# Revit family: Hushwall_2_EN
name_source: partatom
category: Casework
units: mm (PartAtom-declared; Revit-internal decimal feet)

## family parameters
Always vertical = Yes
Cut with Voids When Loaded = No
OmniClass Number = 23.40.35.00
OmniClass Title = Casework
Room Calculation Point = Yes
Shared = No
Work Plane-Based = No

## types (1)
- HUSHWALL
    Assembly Code = E2010200
    Back felt panel = <By Category>
    Back panel = Configuration : Felt panel with TV space
    Bottom element = Bottom element : Blends
    Construction Type = Zdefiniowana konstrukcja
    Default Elevation = 0 mm  [stored 0 ft]
    Depth = 643 mm
    Description = Niezależna przestrzeń do pracy indywidualnej i spotkań, również wirtualnych
    Finish = Zdefiniowane materiały
    Front felt panel = <By Category>
    Front panel = Configuration : Felt panel with TV space
    Height = 1993 mm  [stored 6.53871 ft]
    IfcExportAs = IfcFurniture
    Katalog = https://hushoffice.com
    Konfigurator = https://mikomax.actumwork.pl
    Left side = Configuration2 : None
    Main body = <By Category>
    Manufacturer = Mikomax Smart Office
    Model = Hushwall
    Podstawa jezdna = Cosmos Grey AGC
    Rekomendowany rozmiar monitora = 55”, max. 20 kg
    Right side = Configuration2 : None
    Roleta żaluzjowa = Black GCZ
    Type Image = hushwall.jpg
    URL = https://hushoffice.com
    Width = 1600 mm  [stored 5.24934 ft]

note: [stored X ft] marks values corroborated as IEEE doubles in the binary element streams (Revit-internal decimal feet)

## geometry (parser evidence)
native form markers: Blend x4, Sweep x15
no freeform markers — native parametric forms only
